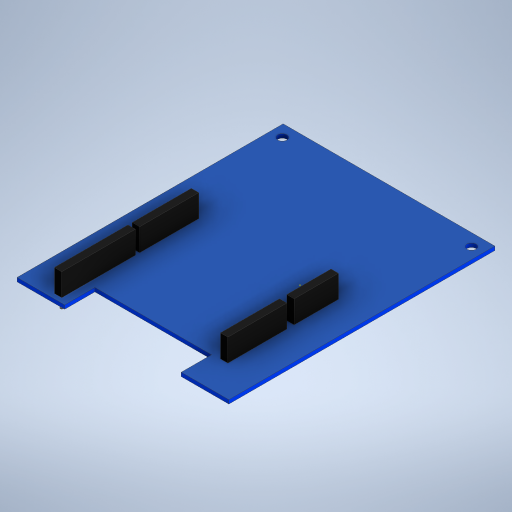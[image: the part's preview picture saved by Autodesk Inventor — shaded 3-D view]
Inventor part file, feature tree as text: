
AUTODESK INVENTOR PART (.ipt)
format: ipt  version: 2023 (Build 270158000, 158)  size: 7,940,096 bytes
history: native  units: mm
features: extrude x5, projected_geometry x4, sketch x3, other x1
ambient origin geometry x8: Origin, YZ Plane, XZ Plane, XY Plane, X Axis, Y Axis, Z Axis, Center Point
bodies: Solide1 (feature_tree)
feature tree (13):
  sketch  "Esquisse1"
  extrude  "Extrusion1"  Depth=91.0mm
  extrude  "Extrusion2"  Depth=3.136339mm
  sketch  "Esquisse2"
  extrude  "Extrusion3"  Depth=1.3mm TaperAngle=0.0deg
  extrude  "Extrusion4"  Depth=9.0mm TaperAngle=0.0deg
  extrude  "Extrusion5"  Depth=1.0mm
  sketch  "Esquisse3"
  other  "Image3"
  projected_geometry  "Boucle projetée1"
  projected_geometry  "Boucle projetée2"
  projected_geometry  "Boucle projetée3"
  projected_geometry  "Boucle projetée4"
